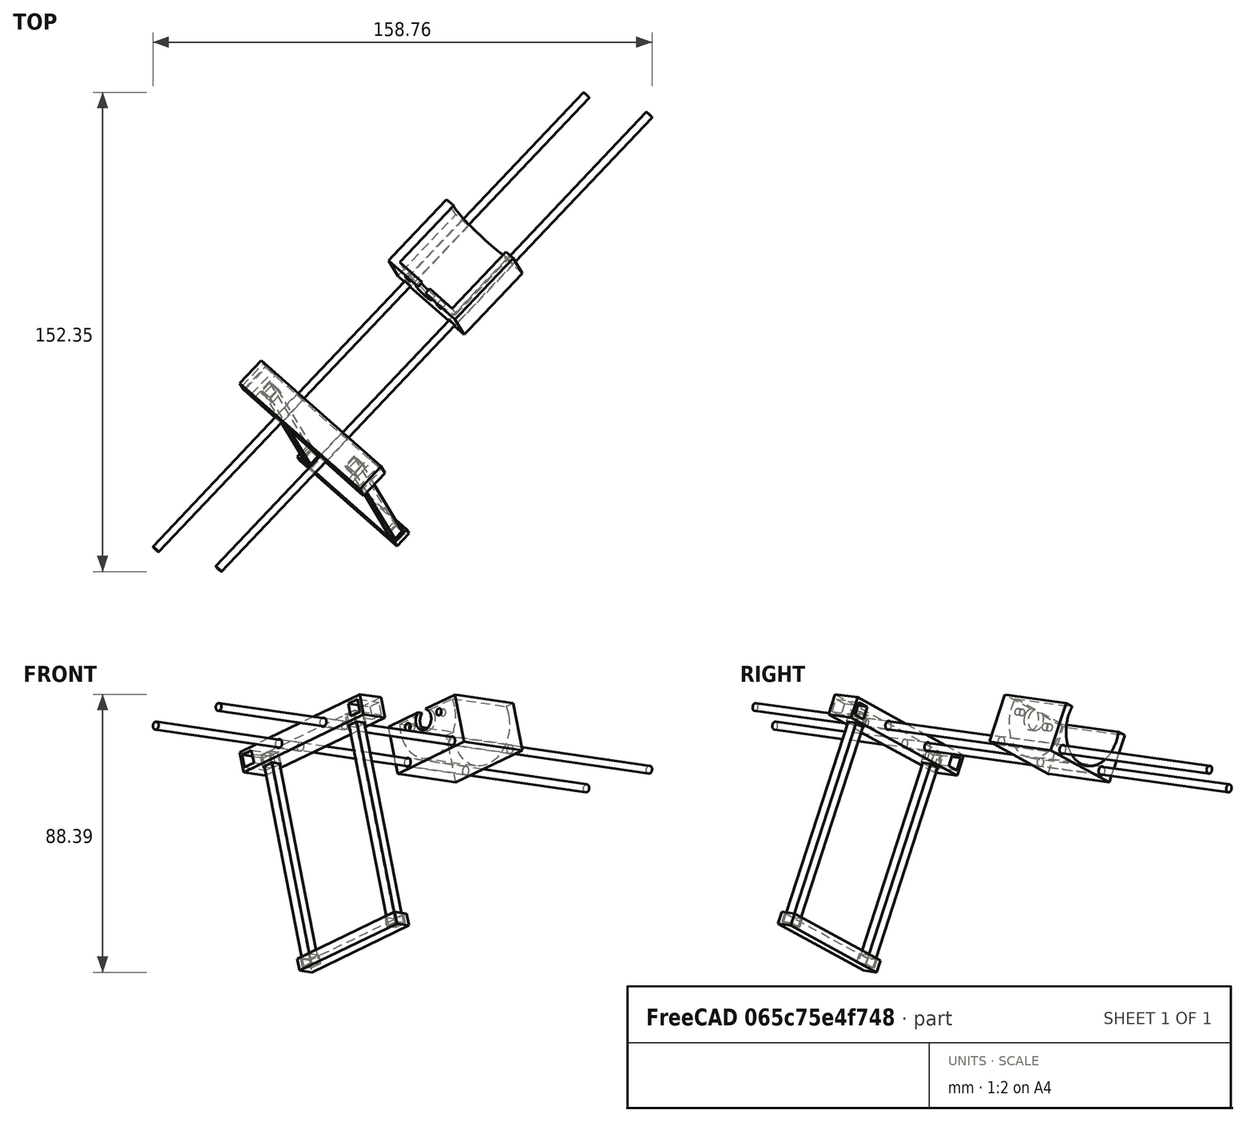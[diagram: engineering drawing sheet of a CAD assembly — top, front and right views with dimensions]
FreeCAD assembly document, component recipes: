
FREECAD ASSEMBLY — COMPONENT RECIPES ("sailface_assembly_v1")

This assembly document has 2 components, labeled P0..P1 below (a component is one placed body or linked part). 0 of them carry a construction recipe — the FreeCAD feature program that regenerates the part from scratch, quoted from this document or its linked companion documents; the rest are supplied as boundary geometry only. No exploded tour is included for this assembly.
COMPONENT P0 — geometry summary ("Servo_SF3218MG001"; no construction recipe available for this part):
  bounding box: 62.8 x 55.7 x 43.1 mm
  tessellated surface: 19,700 triangles
  volume: 32697 mm^3 (22% of its bounding box)
COMPONENT P1 — geometry summary ("Servo_SF3218MG002"; no construction recipe available for this part):
  bounding box: 59.4 x 51.7 x 47.5 mm
  tessellated surface: 19,700 triangles
  volume: 32697 mm^3 (22% of its bounding box)
PROVENANCE & LICENSES
A FreeCAD (.FCStd) document from a public repository crawl; recipes are the document's own serialized feature recipes (and, for linked parts, companion documents' recipes).
License: as declared in the source repository (recorded in the dataset sidecar).
